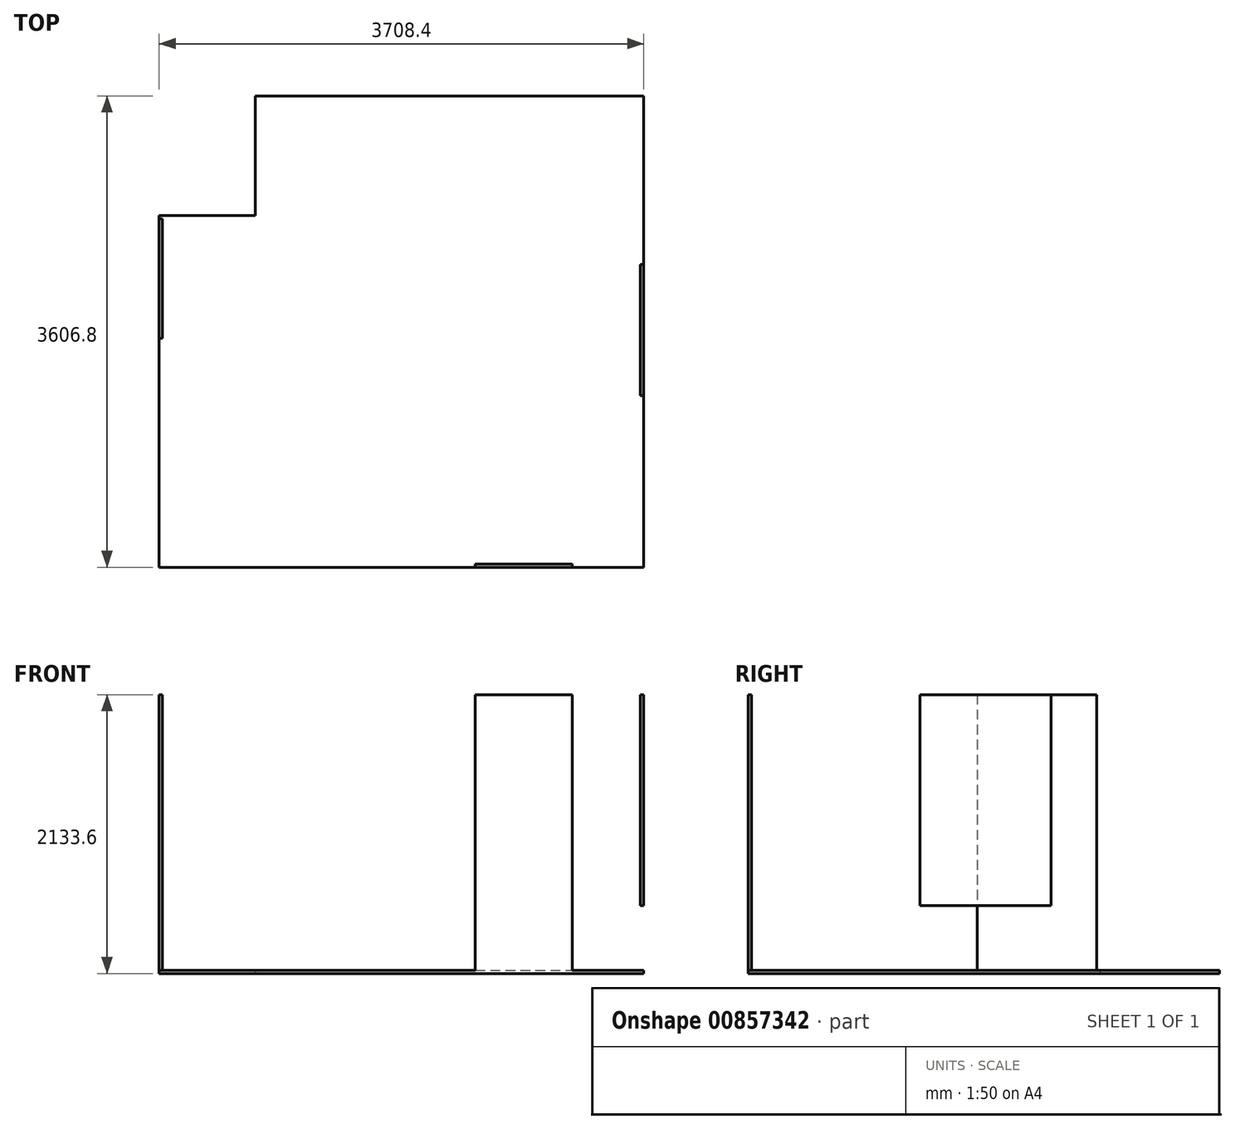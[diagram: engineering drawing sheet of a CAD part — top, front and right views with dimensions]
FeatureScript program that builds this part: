
annotation { "Feature Type Name" : "Feature", "Feature Type Description" : "" }
export const myFeature = defineFeature(function(context is Context, id is Id, definition is map)
    precondition{}
    {
        {
            var Q0;
            Q0=qCreatedBy(makeId("Top.planeOp"),FACE);
            var sketch = newSketch(context, id + "F0", { "sketchPlane" : qUnion([Q0])});
            skLineSegment(sketch, "E0", {"start": v(0, 0) * mm, "end": v(3708.4, 0) * mm});
            skLineSegment(sketch, "E1", {"start": v(3708.4, 0) * mm, "end": v(3708.4, 3606.8) * mm});
            skLineSegment(sketch, "E2", {"start": v(3708.4, 3606.8) * mm, "end": v(736.6, 3606.8) * mm});
            skLineSegment(sketch, "E3", {"start": v(0, 2692.4) * mm, "end": v(0, 0) * mm});
            skLineSegment(sketch, "E4", {"start": v(0, 2692.4) * mm, "end": v(736.6, 2692.4) * mm});
            skLineSegment(sketch, "E5", {"start": v(736.6, 2692.4) * mm, "end": v(736.6, 3606.8) * mm});
            skSolve(sketch);
        }
        {
            var Q0;
            Q0 = qSketchRegion(id + "F0", true);
            var Q1;
            Q1 = qConstructionFilter(qBodyType(qCreatedBy(id + "F0" ,EDGE), BodyType.WIRE), ConstructionObject.NO);
            extrude(context, id + "F1", {"entities" : qUnion([Q0]), "bodyType" : ToolBodyType.SURFACE, "surfaceEntities" : qUnion([Q1]), "depth" : 2438.4 * mm, "offsetDistance" : 25.4 * mm});
        }
        {
            var Q0;
            Q0 = qSketchRegion(id + "F0", true);
            extrude(context, id + "F2", {"entities" : qUnion([Q0]), "depth" : 25.4 * mm, "offsetDistance" : 25.4 * mm});
        }
        {
            var Q0;
            Q0=makeQuery(id+"F1.opExtrude","SWEPT_FACE",FACE,{"disambiguationData":[OSD([sQuery(id+"F0.wireOp",EDGE,"E3")])]});
            var sketch = newSketch(context, id + "F3", { "sketchPlane" : qUnion([Q0])});
            skLineSegment(sketch, "E6", {"start": v(-2667, 0) * mm, "end": v(-2667, 2133.6) * mm});
            skLineSegment(sketch, "E7", {"start": v(-2667, 2133.6) * mm, "end": v(-1752.6, 2133.6) * mm});
            skLineSegment(sketch, "E8", {"start": v(-1752.6, 2133.6) * mm, "end": v(-1752.6, 0) * mm});
            skLineSegment(sketch, "E9", {"start": v(-1752.6, 0) * mm, "end": v(-2667, 0) * mm});
            skSolve(sketch);
        }
        {
            var Q0;
            Q0 = qSketchRegion(id + "F3", true);
            extrude(context, id + "F4", {"entities" : qUnion([Q0]), "operationType" : NewBodyOperationType.ADD, "oppositeDirection" : true, "depth" : 25.4 * mm, "offsetDistance" : 25.4 * mm});
        }
        {
            var Q0;
            Q0=makeQuery(id+"F1.opExtrude","SWEPT_FACE",FACE,{"disambiguationData":[OSD([sQuery(id+"F0.wireOp",EDGE,"E0")])]});
            var sketch = newSketch(context, id + "F5", { "sketchPlane" : qUnion([Q0])});
            skLineSegment(sketch, "E10", {"start": v(3162.3, 0) * mm, "end": v(3162.3, 2133.6) * mm});
            skLineSegment(sketch, "E11", {"start": v(3162.3, 2133.6) * mm, "end": v(2419.35, 2133.6) * mm});
            skLineSegment(sketch, "E12", {"start": v(2419.35, 2133.6) * mm, "end": v(2419.35, 0) * mm});
            skLineSegment(sketch, "E13", {"start": v(2419.35, 0) * mm, "end": v(3162.3, 0) * mm});
            skSolve(sketch);
        }
        {
            var Q0;
            Q0 = qSketchRegion(id + "F5", true);
            extrude(context, id + "F6", {"entities" : qUnion([Q0]), "operationType" : NewBodyOperationType.ADD, "oppositeDirection" : true, "depth" : 25.4 * mm, "offsetDistance" : 25.4 * mm});
        }
        {
            var Q0;
            Q0=makeQuery(id+"F1.opExtrude","SWEPT_FACE",FACE,{"disambiguationData":[OSD([sQuery(id+"F0.wireOp",EDGE,"E1")])]});
            var sketch = newSketch(context, id + "F7", { "sketchPlane" : qUnion([Q0])});
            skLineSegment(sketch, "E14.bottom", {"start": v(2317.75, 2133.6) * mm, "end": v(1314.45, 2133.6) * mm});
            skLineSegment(sketch, "E14.top", {"start": v(2317.75, 520.7) * mm, "end": v(1314.45, 520.7) * mm});
            skLineSegment(sketch, "E14.left", {"start": v(2317.75, 2133.6) * mm, "end": v(2317.75, 520.7) * mm});
            skLineSegment(sketch, "E14.right", {"start": v(1314.45, 2133.6) * mm, "end": v(1314.45, 520.7) * mm});
            skSolve(sketch);
        }
        {
            var Q0;
            Q0 = qSketchRegion(id + "F7", true);
            extrude(context, id + "F8", {"entities" : qUnion([Q0]), "oppositeDirection" : true, "depth" : 25.4 * mm, "offsetDistance" : 25.4 * mm});
        }
    });
